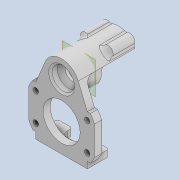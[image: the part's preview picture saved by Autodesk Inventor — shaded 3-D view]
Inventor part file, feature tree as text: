
AUTODESK INVENTOR PART (.ipt)
format: ipt  version: 2020 (Build 240168000, 168)  size: 501,248 bytes
history: native  units: mm
features: extrude x15, sketch x15, reference x11, projected_geometry x10, other x6, fillet x5, chamfer x4, plane x3, thicken_offset x2
ambient origin geometry x8: Origin, YZ Plane, XZ Plane, XY Plane, X Axis, Y Axis, Z Axis, Center Point
bodies: Solid1 (feature_tree)
feature tree (71):
  extrude  "Extrusion1"  Depth=12.0mm
  extrude  "Extrusion2"  Depth=12.0mm
  extrude  "Extrusion3"  Depth=2.2mm
  plane  "Work Plane1"
  extrude  "Extrusion4"  Depth=10.0mm
  chamfer  "Chamfer1"  Distance=2.0mm
  extrude  "Extrusion5"  Depth=4.8mm TaperAngle=0.0deg
  extrude  "Extrusion6"  Depth=4.8mm TaperAngle=0.0deg
  extrude  "Extrusion7"  Depth=1.0mm
  plane  "Work Plane2"
  sketch  "Sketch10"  dims[d18=2.8mm d19=0.0mm d20=1.0mm d21=2.0mm d22=45.0deg]
  plane  "Work Plane4"
  extrude  "Extrusion10"  Depth=1.0mm TaperAngle=45.0deg
  extrude  "Extrusion11"  Depth=14.3mm
  fillet  "Fillet1"  Radius=1.8mm
  fillet  "Fillet2"  Radius=2.8mm
  extrude  "Extrusion13"  Depth=4.0mm TaperAngle=0.0deg
  extrude  "Extrusion14"  Depth=4.0mm
  fillet  "Fillet5"  Radius=8.37758mm
  chamfer  "Chamfer2"  Distance=4.0mm
  thicken_offset  "Thicken1"
  thicken_offset  "Thicken2"
  chamfer  "Chamfer5"  Distance=2.0mm
  extrude  "Extrusion15"  Depth=4.5mm
  extrude  "Extrusion18"  Depth=4.5mm
  fillet  "Fillet8"  Radius=4.0mm
  fillet  "Fillet9"  Radius=6.0mm
  extrude  "Extrusion19"  Depth=3.0mm
  extrude  "Extrusion20"  Depth=4.5mm TaperAngle=0.0deg
  chamfer  "Chamfer6"  Distance=1.5mm
  sketch  "Sketch1"  dims[d0=4.0mm d1=12.0mm]
  reference  "Reference1"
  reference  "Reference2"
  sketch  "Sketch2"  dims[d2=4.0mm d3=12.0mm]
  projected_geometry  "Projected Loop1"
  sketch  "Sketch3"  dims[d4=16.0mm d5=2.2mm]
  projected_geometry  "Projected Loop2"
  sketch  "Sketch4"  dims[d6=6.0mm d7=10.0mm d8=2.0mm d9=0.0mm]
  sketch  "Sketch5"  dims[d10=8.5mm d11=4.8mm d12=0.0mm]
  projected_geometry  "Projected Loop3"
  sketch  "Sketch6"  dims[d13=3.9mm d14=4.8mm d15=0.0mm]
  projected_geometry  "Projected Loop4"
  sketch  "Sketch7"  dims[d16=-2.0mm d17=1.0mm]
  reference  "Reference3"
  reference  "Reference4"
  reference  "Reference7"
  sketch  "Sketch11"  dims[d23=10.3mm d24=14.3mm d25=1.8mm d26=2.8mm d27=0.0mm]
  reference  "Reference8"
  sketch  "Sketch13"  dims[d28=4.0mm d29=0.0mm d30=4.0mm d31=0.0mm]
  projected_geometry  "Projected Loop9"
  sketch  "Sketch14"  dims[d42=4.0mm d43=0.0mm d44=4.0mm d45=8.37758mm]
  projected_geometry  "Projected Loop10"
  reference  "Reference10"
  sketch  "Sketch15"  dims[d46=1.2mm]
  projected_geometry  "Projected Loop11"
  projected_geometry  "Projected Loop12"
  sketch  "Sketch18"  dims[d47=4.0mm]
  reference  "Reference13"
  reference  "Reference14"
  reference  "Reference15"
  reference  "Reference16"
  sketch  "Sketch19"  dims[d48=8.37758mm]
  projected_geometry  "Projected Loop13"
  sketch  "Sketch20"  dims[d49=1.2mm d50=4.0mm d51=0.0mm d52=2.0mm d53=1.5mm d59=20.0mm d60=4.0mm d61=0.0mm d62=6.0mm d63=3.0mm d64=4.0mm d65=0.0mm d66=1.5mm d67=0.5mm d68=2.0mm d69=45.0deg d73=0.1mm d74=0.15mm d75=0.1mm d76=0.15mm d80=0.5mm d81=2.0mm d82=45.0deg d83=6.0mm d84=0.0mm d93=2.8mm d94=2.8mm d95=6.0mm d96=0.0mm d97=2.0mm d98=1.0mm d99=1.4mm d100=1.4mm d101=4.5mm d102=0.0mm d103=0.25mm d104=7.0mm d105=0.0mm d106=0.25mm d107=2.0mm d108=45.0deg]
  projected_geometry  "Projected Loop14"
  parser-record x1  (decoder bookkeeping rows leaked as tree rows — omitted from the tree; the rows remain in map.json)
  other  "tip_ass_t1.iam"
  other  "motor_1608:1"
  other  "motor_1608_inner:1"
  other  "motor_1608_outer:1"
  other  "pin_conn_2:1"
note: 1 file-system path scrubbed to <path> (originals preserved in map.json)
